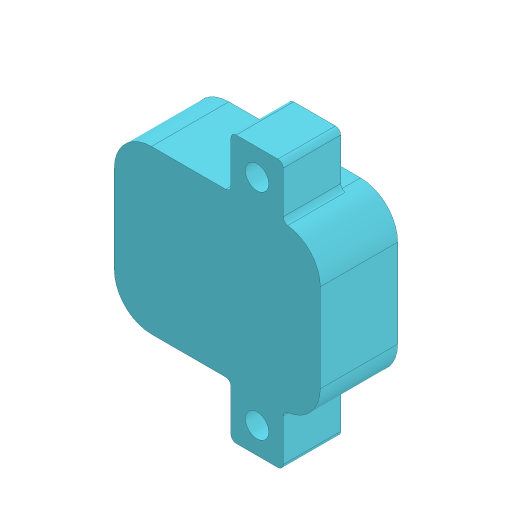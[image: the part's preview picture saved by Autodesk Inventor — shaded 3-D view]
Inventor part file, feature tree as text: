
AUTODESK INVENTOR PART (.ipt)
format: ipt  version: 2024.3 (Build 283343000, 343)  size: 480,768 bytes
history: native  units: mm
features: sketch x6, projected_geometry x6, extrude x5, reference x5, other x3, fillet x2, hole x1
ambient origin geometry x8: Origin, YZ Plane, XZ Plane, XY Plane, X Axis, Y Axis, Z Axis, Center Point
bodies: Solid1 (feature_tree)
feature tree (28):
  extrude  "Extrusion1"  Depth=4.0mm
  extrude  "Extrusion2"  Depth=2.0mm
  extrude  "Extrusion3"  Depth=9.8mm
  extrude  "Extrusion4"  Depth=2.4mm
  hole  "Hole1"  [1 undecoded]
  fillet  "Fillet1"  Radius=10.0mm
  fillet  "Fillet2"  Radius=11.0mm
  extrude  "Extrusion5"  Depth=1.0mm
  sketch  "Sketch1"  dims[d0=0.6mm d1=4.0mm]
  reference  "Reference1"
  sketch  "Sketch2"  dims[d2=5.0mm d3=0.0mm d4=2.0mm]
  reference  "Reference2"
  projected_geometry  "Projected Loop1"
  reference  "Reference3"
  sketch  "Sketch3"  dims[d5=9.8mm d6=0.0mm d7=3.15mm]
  reference  "Reference4"
  reference  "Reference5"
  sketch  "Sketch4"  dims[d8=2.4mm d9=2.4mm]
  projected_geometry  "Projected Loop2"
  sketch  "Sketch5"  dims[d10=3.0mm d11=0.0mm d12=10.0mm d13=10.0mm d14=11.0mm d15=0.0mm]
  projected_geometry  "Projected Loop3"
  projected_geometry  "Projected Loop4"
  projected_geometry  "Projected Loop5"
  sketch  "Sketch6"  dims[d16=4.5mm d17=6.0mm d18=7.5mm d19=4.775mm d20=90.0deg d21=8.0mm d22=20.594885mm d23=1.0mm d24=1.0mm d25=11.0mm d26=0.0mm]
  projected_geometry  "Projected Loop6"
  parser-record x1  (decoder bookkeeping rows leaked as tree rows — omitted from the tree; the rows remain in map.json)
  other  "PrzyciskSTOP.iam"
  other  "DF Robot DFR0029-R:1"
note: 1 required parameter value undecoded (feature->parameter linkage not recoverable at this tier; creation-order binding heuristic only, values carry confidence <= 0.55)
note: 1 file-system path scrubbed to <path> (originals preserved in map.json)
